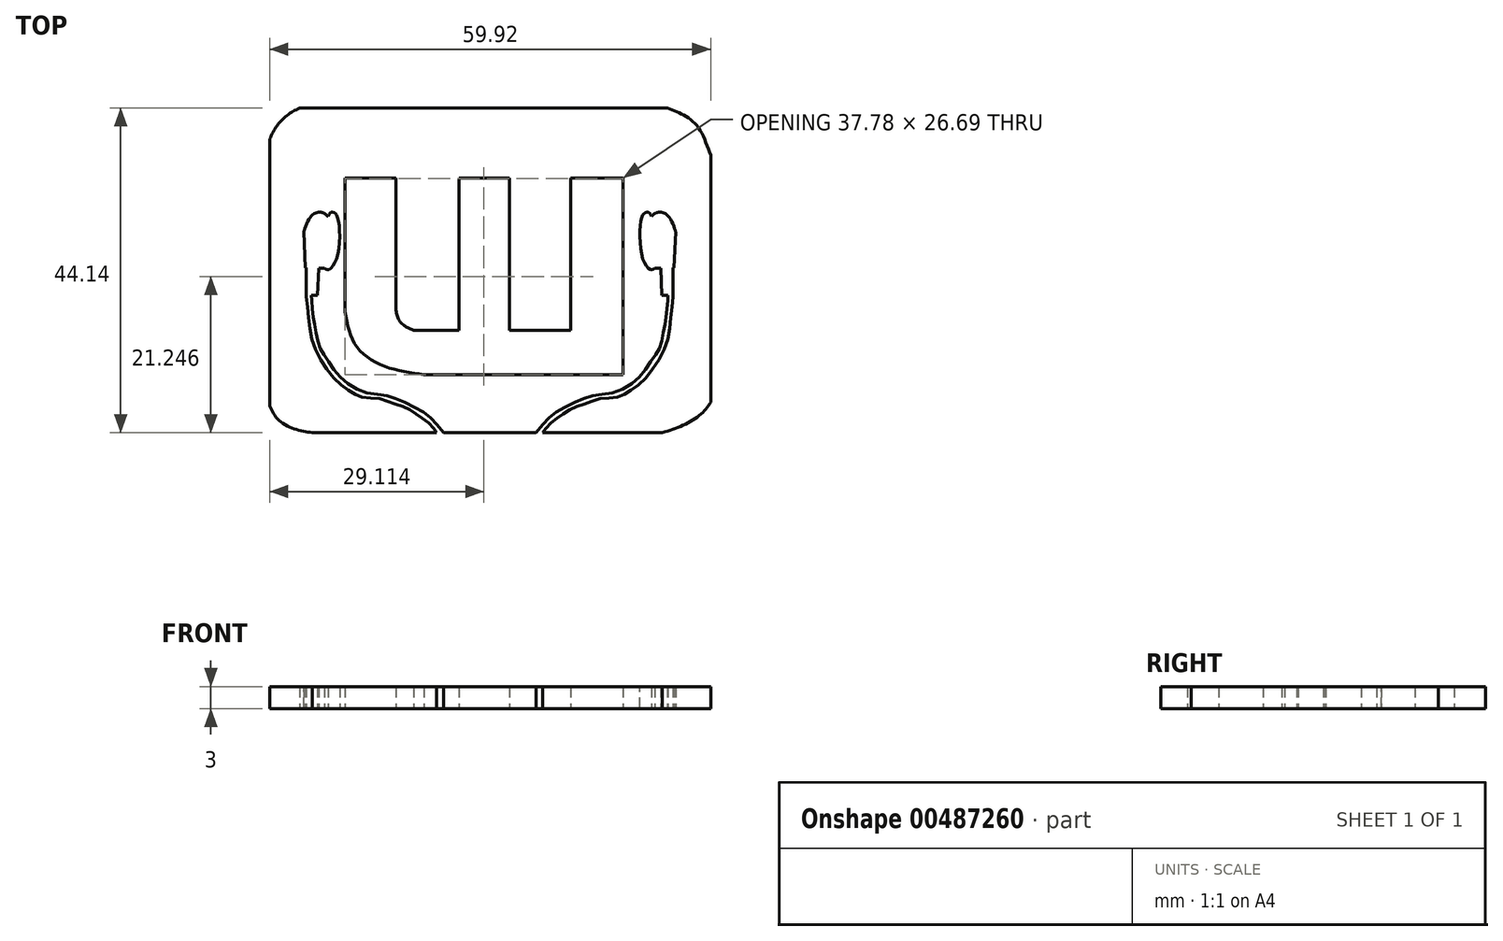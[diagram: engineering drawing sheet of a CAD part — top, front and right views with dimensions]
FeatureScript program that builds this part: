
annotation { "Feature Type Name" : "Feature", "Feature Type Description" : "" }
export const myFeature = defineFeature(function(context is Context, id is Id, definition is map)
    precondition{}
    {
        {
            var Q0;
            Q0=qCreatedBy(makeId("Top.planeOp"),FACE);
            var sketch = newSketch(context, id + "F0", { "sketchPlane" : qUnion([Q0])});
            skLineSegment(sketch, "E0", {"start": v(-23.27, 20.65) * mm, "end": v(-16.36, 20.65) * mm});
            skLineSegment(sketch, "E1", {"start": v(-16.36, 20.65) * mm, "end": v(-16.36, 2.88) * mm});
            skLineSegment(sketch, "E2", {"start": v(-23.27, 20.65) * mm, "end": v(-23.27, 2.53) * mm});
            skLineSegment(sketch, "E3", {"start": v(-7.77, 20.65) * mm, "end": v(-0.9, 20.65) * mm});
            skLineSegment(sketch, "E4", {"start": v(-7.77, 20.65) * mm, "end": v(-7.77, 0) * mm});
            skLineSegment(sketch, "E5", {"start": v(-7.77, 0) * mm, "end": v(-13.93, 0) * mm});
            skLineSegment(sketch, "E6", {"start": v(-0.9, 20.65) * mm, "end": v(-0.9, 0) * mm});
            skLineSegment(sketch, "E7", {"start": v(-0.9, 0) * mm, "end": v(7.4, 0) * mm});
            skLineSegment(sketch, "E8", {"start": v(7.4, 0) * mm, "end": v(7.4, 20.65) * mm});
            skFitSpline(sketch, "E9", {"points": [v(-16.36, 2.88) * mm, v(-15.93, 1.4) * mm, v(-14.89, 0.42) * mm, v(-13.93, 0) * mm], "startDerivative": vector(0.71, -4.4) * mm, "endDerivative": vector(3.18, -1.17) * mm});
            skLineSegment(sketch, "E10", {"start": v(7.4, 20.65) * mm, "end": v(14.51, 20.65) * mm});
            skLineSegment(sketch, "E11", {"start": v(14.51, 20.65) * mm, "end": v(14.51, -6.04) * mm});
            skFitSpline(sketch, "E12", {"points": [v(-23.27, 2.53) * mm, v(-21.8, -2.05) * mm, v(-17.87, -4.91) * mm, v(-12.51, -6.04) * mm], "startDerivative": vector(2.7, -15.14) * mm, "endDerivative": vector(15.86, -2.1) * mm});
            skLineSegment(sketch, "E13", {"start": v(-12.51, -6.04) * mm, "end": v(14.51, -6.04) * mm});
            skLineSegment(sketch, "E14", {"start": v(-29.45, 30.2) * mm, "end": v(20.55, 30.2) * mm});
            skLineSegment(sketch, "E15", {"start": v(-33.49, 25.99) * mm, "end": v(-33.49, -10.3) * mm});
            skLineSegment(sketch, "E16", {"start": v(-27.73, -13.94) * mm, "end": v(20.55, -13.94) * mm});
            skFitSpline(sketch, "E17", {"points": [v(-33.49, 25.99) * mm, v(-32.54, 27.73) * mm, v(-31.01, 29.29) * mm, v(-29.45, 30.2) * mm], "startDerivative": vector(2.48, 5.33) * mm, "endDerivative": vector(4.96, 2.5) * mm});
            skFitSpline(sketch, "E18", {"points": [v(-27.73, -13.94) * mm, v(-30.03, -13.45) * mm, v(-32.37, -12.14) * mm, v(-33.49, -10.3) * mm], "startDerivative": vector(-6.83, 1.06) * mm, "endDerivative": vector(-2.77, 6.24) * mm});
            skLineSegment(sketch, "E19", {"start": v(26.43, 23.79) * mm, "end": v(26.43, -10.21) * mm});
            skFitSpline(sketch, "E20", {"points": [v(19.85, -13.94) * mm, v(22.8, -12.86) * mm, v(25.23, -11.3) * mm, v(26.43, -9.8) * mm], "startDerivative": vector(8.2, 2.62) * mm, "endDerivative": vector(3.62, 5.37) * mm});
            skFitSpline(sketch, "E21", {"points": [v(20.55, 30.2) * mm, v(22.75, 29.26) * mm, v(24.84, 27.44) * mm, v(26.43, 23.79) * mm], "startDerivative": vector(7.38, -2.64) * mm, "endDerivative": vector(3.74, -9.5) * mm});
            skFitSpline(sketch, "E22", {"points": [v(18.38, 15.45) * mm, v(18.92, 15.91) * mm, v(19.77, 16.02) * mm, v(20.9, 15.2) * mm, v(21.68, 13.36) * mm, v(21.67, 13.36) * mm], "startDerivative": vector(2.5, 2.82) * mm, "endDerivative": vector(-0.22, 0.11) * mm});
            skLineSegment(sketch, "E23", {"start": v(21.68, 13.36) * mm, "end": v(21.47, 8.47) * mm});
            skLineSegment(sketch, "E24", {"start": v(21.47, 8.47) * mm, "end": v(21.33, 8.48) * mm});
            skLineSegment(sketch, "E25", {"start": v(21.33, 8.48) * mm, "end": v(21.33, 4.56) * mm});
            skFitSpline(sketch, "E26", {"points": [v(21.33, 4.56) * mm, v(21, 1.51) * mm, v(20.45, -1.72) * mm, v(18.88, -4.83) * mm, v(16.78, -7.3) * mm, v(15.07, -8.5) * mm, v(13.63, -9.14) * mm, v(11.47, -9.3) * mm, v(9.6, -9.9) * mm, v(7.98, -10.48) * mm, v(6.6, -11.28) * mm, v(5.31, -12.14) * mm, v(4.1, -13.24) * mm, v(3.61, -13.94) * mm], "startDerivative": vector(-3.63, -32.4) * mm, "endDerivative": vector(-8.41, -13.6) * mm});
            skFitSpline(sketch, "E27", {"points": [v(18.38, 15.45) * mm, v(18, 16.02) * mm, v(17.58, 16) * mm, v(17.06, 15.28) * mm, v(17.2, 9.77) * mm, v(18.38, 8.2) * mm, v(18.86, 8.43) * mm], "startDerivative": vector(-2.75, 6.02) * mm, "endDerivative": vector(4.1, 3.54) * mm});
            skLineSegment(sketch, "E28", {"start": v(18.86, 8.43) * mm, "end": v(19.65, 8.43) * mm});
            skFitSpline(sketch, "E29", {"points": [v(2.68, -13.94) * mm, v(4.36, -12.03) * mm, v(6.06, -10.78) * mm, v(8.7, -9.49) * mm, v(10.68, -8.84) * mm, v(13.3, -8.49) * mm, v(15.9, -7.1) * mm, v(17.56, -5.38) * mm, v(18.75, -3.6) * mm, v(19.51, -2.4) * mm, v(19.9, -0.85) * mm, v(20.24, 0.95) * mm, v(20.45, 2.35) * mm, v(20.6, 4.18) * mm, v(20.63, 4.75) * mm], "startDerivative": vector(20.65, 25.36) * mm, "endDerivative": vector(0.6, 12.21) * mm});
            skLineSegment(sketch, "E30", {"start": v(20.63, 4.75) * mm, "end": v(19.82, 4.75) * mm});
            skLineSegment(sketch, "E31", {"start": v(19.82, 4.75) * mm, "end": v(19.65, 8.43) * mm});
            skLineSegment(sketch, "E32", {"start": v(2.68, -13.94) * mm, "end": v(-9.12, -13.94) * mm, "construction": true});
            skLineSegment(sketch, "E33", {"start": v(-3.59, -13.94) * mm, "end": v(-3.59, 32.39) * mm, "construction": true});
            skFitSpline(sketch, "E34.MirrorCS", {"points": [v(-25.56, 15.45) * mm, v(-25.18, 16.02) * mm, v(-24.75, 16) * mm, v(-24.24, 15.28) * mm, v(-24.38, 9.77) * mm, v(-25.56, 8.2) * mm, v(-26.04, 8.43) * mm], "startDerivative": vector(2.75, 6.02) * mm, "endDerivative": vector(-4.1, 3.54) * mm});
            skFitSpline(sketch, "E35.MirrorCS", {"points": [v(-25.56, 15.45) * mm, v(-26.1, 15.91) * mm, v(-26.95, 16.02) * mm, v(-28.08, 15.2) * mm, v(-28.86, 13.36) * mm, v(-28.85, 13.36) * mm], "startDerivative": vector(-2.5, 2.82) * mm, "endDerivative": vector(0.22, 0.11) * mm});
            skLineSegment(sketch, "E36.MirrorCS", {"start": v(-26.04, 8.43) * mm, "end": v(-26.83, 8.43) * mm});
            skLineSegment(sketch, "E37.MirrorCS", {"start": v(-27, 4.75) * mm, "end": v(-26.83, 8.43) * mm});
            skLineSegment(sketch, "E38.MirrorCS", {"start": v(-28.5, 8.48) * mm, "end": v(-28.5, 4.56) * mm});
            skLineSegment(sketch, "E39.MirrorCS", {"start": v(-28.86, 13.36) * mm, "end": v(-28.65, 8.47) * mm});
            skLineSegment(sketch, "E40.MirrorCS", {"start": v(-28.65, 8.47) * mm, "end": v(-28.5, 8.48) * mm});
            skFitSpline(sketch, "E41.MirrorCS", {"points": [v(-28.5, 4.56) * mm, v(-28.18, 1.51) * mm, v(-27.63, -1.72) * mm, v(-26.06, -4.83) * mm, v(-23.96, -7.3) * mm, v(-22.25, -8.5) * mm, v(-20.81, -9.14) * mm, v(-18.65, -9.3) * mm, v(-16.79, -9.9) * mm, v(-15.16, -10.48) * mm, v(-13.78, -11.28) * mm, v(-12.5, -12.14) * mm, v(-11.29, -13.24) * mm, v(-10.79, -13.94) * mm], "startDerivative": vector(3.63, -32.4) * mm, "endDerivative": vector(8.41, -13.6) * mm});
            skFitSpline(sketch, "E42.MirrorCS", {"points": [v(-9.86, -13.94) * mm, v(-11.54, -12.03) * mm, v(-13.24, -10.78) * mm, v(-15.88, -9.49) * mm, v(-17.86, -8.84) * mm, v(-20.47, -8.49) * mm, v(-23.07, -7.1) * mm, v(-24.74, -5.38) * mm, v(-25.93, -3.6) * mm, v(-26.7, -2.4) * mm, v(-27.07, -0.85) * mm, v(-27.42, 0.95) * mm, v(-27.63, 2.35) * mm, v(-27.77, 4.18) * mm, v(-27.8, 4.75) * mm], "startDerivative": vector(-20.65, 25.36) * mm, "endDerivative": vector(-0.6, 12.21) * mm});
            skLineSegment(sketch, "E43.MirrorCS", {"start": v(-27.8, 4.75) * mm, "end": v(-27, 4.75) * mm});
            skSolve(sketch);
        }
        {
            var Q0;
            Q0=makeQuery(id+"F0.imprint","IMPRINT",FACE,{"disambiguationData":[TD([[makeQuery(id+"F0.imprint","IMPRINT",EDGE,{"derivedFrom":sQuery(id+"F0.wireOp",EDGE,"E0")}),1.0]])]});
            extrude(context, id + "F1", {"entities" : qUnion([Q0]), "depth" : 3 * mm});
        }
    });
